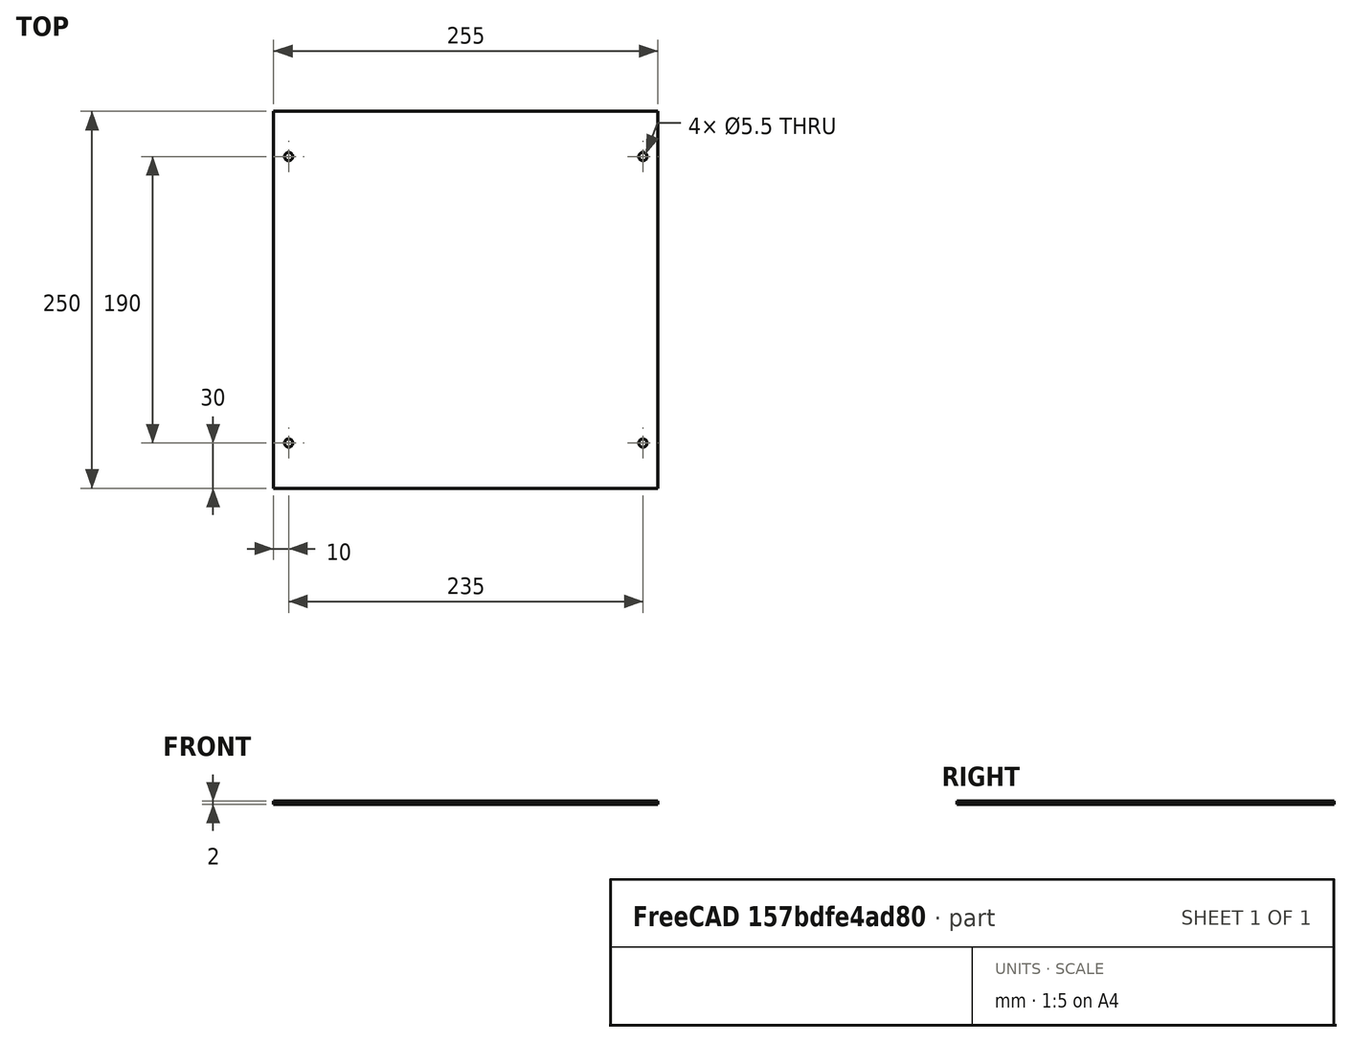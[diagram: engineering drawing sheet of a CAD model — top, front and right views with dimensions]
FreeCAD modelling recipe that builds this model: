
FCSTD DOCUMENT  (FreeCAD 0.15R4671 (Git))
Label: back
License: All rights reserved
LicenseURL: http://en.wikipedia.org/wiki/All_rights_reserved
objects: Drawing::FeatureViewPython×5, Part::Cylinder×4, Part::Cut×4, Part::Box×1, Drawing::FeatureViewPart×1, Drawing::FeaturePage×1
note: 9 computed .brp shape members not serialized (recipe doc carries the construction recipe); baked Part::Feature solids carry a one-line shape summary decoded from their .brp

FEATURE [Part::Box] Box001  label="Cube001"
  Height = 2
  Length = 255
  Placement = pos=(0,0,1.5332e-08) rot=(0,0,1;0rad)
  Width = 250
FEATURE [Part::Cylinder] Cylinder004
  Angle = 360
  Height = 10
  Placement = pos=(10,30,-5) rot=(0,0,1;0rad)
  Radius = 2.75
FEATURE [Part::Cylinder] Cylinder005
  Angle = 360
  Height = 10
  Placement = pos=(10,220,-5) rot=(0,0,1;0rad)
  Radius = 2.75
FEATURE [Part::Cylinder] Cylinder006
  Angle = 360
  Height = 10
  Placement = pos=(245,30,-5) rot=(0,0,1;0rad)
  Radius = 2.75
FEATURE [Part::Cylinder] Cylinder007
  Angle = 360
  Height = 10
  Placement = pos=(245,220,-5) rot=(0,0,1;0rad)
  Radius = 2.75
FEATURE [Part::Cut] Cut004
  Base = -> Box001
  Tool = -> Cylinder004
FEATURE [Part::Cut] Cut005
  Base = -> Cut004
  Tool = -> Cylinder005
FEATURE [Part::Cut] Cut006
  Base = -> Cut005
  Tool = -> Cylinder006
FEATURE [Part::Cut] Cut007  label="back"
  Base = -> Cut006
  Tool = -> Cylinder007
FEATURE [Drawing::FeatureViewPart] Ortho  label="Ortho_0_0"
  Direction = (0,0,-1)
  HiddenWidth = 0.15
  LineWidth = 0.35
  Rotation = 180
  Scale = 0.5
  ShowHiddenLines = false
  ShowSmoothLines = false
  Source = -> Cut007
  Tolerance = 0.05
  ViewResult = <g id="Ortho_0_0"\n   transform="rotate(180,46.25,56) translate(46.25,56) scale(0.5,0.5)"\n  >\n<g   stroke="rgb(0, 0, 0)"\n   stroke-width="0.7"\n   stroke-linecap="butt"\n   stroke-linejoin="miter"\n   fill="none"\n   transform="scale(1,-1)"\n  >\n<path id= "1" d=" M 0 0 L 0 250 " />\n<path id= "2" d=" M 0 0 L -255 0 " />\n<path id= "3" d=" M 0 250 L -255 250 " />\n<path id= "4" d=" M -255 0 L -255 250 " />\n<circle cx ="-245" cy ="220" r ="2.75" /><circle cx ="-10" cy ="220" r ="2.75" /><circle cx ="-245" cy ="30" r ="2.75" /><circle cx ="-10" cy ="30" r ="2.75" /></g>\n</g>
  Visible = true
  X = 46.25
  Y = 56
FEATURE [Drawing::FeatureViewPython] dimStack001  # drawing view (typed FeaturePython)
  Rotation = 0
  ViewResult = <g> <line x1="51.250000" y1="169.375001" x2="51.250000" y2="198.365725" style="stroke:rgb(0,0,255);stroke-width:0.50" />\n<line x1="46.250000" y1="183.000001" x2="46.250000" y2="198.365725" style="stroke:rgb(0,0,255);stroke-width:0.50" />\n<line x1="51.250000" y1="197.365725" x2="46.250000" y2="197.365725" style="stroke:rgb(0,0,255);stroke-width:0.50" />\n<polygon points="51.250000,197.365725 54.250000,198.365725 55.250000,197.365725 54.250000,196.365725" style="fill:rgb(0,0,255);stroke:rgb(0,0,255);stroke-width:0" />\n<polygon points="46.250000,197.365725 43.250000,196.365725 42.250000,197.365725 43.250000,198.365725" style="fill:rgb(0,0,255);stroke:rgb(0,0,255);stroke-width:0" />\n<text x="48.750000" y="195.365725" font-family="inherit" font-size="3.6" fill="rgb(0,0,255)" text-anchor="middle" transform="rotate(0.000000 48.750000,195.365725)" >10</text> </g> 
  Visible = true
  X = 0
  Y = 0
  arrowL1 = 3
  arrowL2 = 1
  arrowW = 2
  arrow_scheme = 0
  autoPlaceOffset = 2
  click1_x = 47.0563
  click1_y = 197.366
  comma_decimal_place = false
  dimension_line_overshoot = 1
  gap_datum_points = 2
  lineColor = rgb(0,0,255)
  stack_offset = 7
  stack_offset0 = 0
  strokeWidth = 0.5
  textFormat_linear = %(value)f
  textRenderer_color = rgb(0,0,255)
  textRenderer_family = inherit
  textRenderer_size = 3.6
  unit_custom_scale = 1
  unit_scheme = 0
FEATURE [Drawing::FeatureViewPython] dimStack002  # drawing view (typed FeaturePython)
  Rotation = 0
  ViewResult = <g> <line x1="49.249999" y1="166.000000" x2="33.981770" y2="166.000000" style="stroke:rgb(0,0,255);stroke-width:0.50" />\n<line x1="44.249999" y1="181.000000" x2="33.981770" y2="181.000000" style="stroke:rgb(0,0,255);stroke-width:0.50" />\n<line x1="34.981770" y1="166.000000" x2="34.981770" y2="181.000000" style="stroke:rgb(0,0,255);stroke-width:0.50" />\n<polygon points="34.981770,166.000000 33.981770,169.000000 34.981770,170.000000 35.981770,169.000000" style="fill:rgb(0,0,255);stroke:rgb(0,0,255);stroke-width:0" />\n<polygon points="34.981770,181.000000 35.981770,178.000000 34.981770,177.000000 33.981770,178.000000" style="fill:rgb(0,0,255);stroke:rgb(0,0,255);stroke-width:0" />\n<text x="32.981770" y="173.500000" font-family="inherit" font-size="3.6" fill="rgb(0,0,255)" text-anchor="middle" transform="rotate(-90.000000 32.981770,173.500000)" >30</text> </g> 
  Visible = true
  X = 0
  Y = 0
  arrowL1 = 3
  arrowL2 = 1
  arrowW = 2
  arrow_scheme = 0
  autoPlaceOffset = 2
  click1_x = 34.9818
  click1_y = 177.703
  comma_decimal_place = false
  dimension_line_overshoot = 1
  gap_datum_points = 2
  lineColor = rgb(0,0,255)
  stack_offset = 7
  stack_offset0 = 0
  strokeWidth = 0.5
  textFormat_linear = %(value)f
  textRenderer_color = rgb(0,0,255)
  textRenderer_family = inherit
  textRenderer_size = 3.6
  unit_custom_scale = 1
  unit_scheme = 0
FEATURE [Drawing::FeatureViewPython] dia001  # drawing view (typed FeaturePython)
  Rotation = 0
  ViewResult = <g>  <circle cx ="51.250000" cy ="71.000000" r="0.250000" stroke="none" fill="rgb(0,0,255)" /> \n<line x1="73.427542" y1="70.089927" x2="49.876156" y2="71.056377" style="stroke:rgb(0,0,255);stroke-width:0.50" />\n<polygon points="52.623844,70.943623 55.662322,71.819778 56.620480,70.779618 55.580320,69.821460" style="fill:rgb(0,0,255);stroke:rgb(0,0,255);stroke-width:0" />\n<polygon points="49.876156,71.056377 46.837678,70.180222 45.879520,71.220382 46.919680,72.178540" style="fill:rgb(0,0,255);stroke:rgb(0,0,255);stroke-width:0" />\n<line x1="73.427542" y1="70.089927" x2="78.619389" y2="70.089927" style="stroke:rgb(0,0,255);stroke-width:0.50" />\n<text x="76.023466" y="68.089927" font-family="inherit" font-size="3.6" fill="rgb(0,0,255)" text-anchor="middle" transform="rotate(0.000000 76.023466,68.089927)" >Ø5.5</text> </g>
  Visible = true
  X = 0
  Y = 0
  arrowL1 = 3
  arrowL2 = 1
  arrowW = 2
  arrow_scheme = 0
  autoPlaceOffset = 2
  autoPlaceText = true
  centerPointDia = 0.5
  click1_x = 73.4275
  click1_y = 70.0899
  click2_x = 78.6194
  click2_y = 71.9442
  click3_x = 78.6194
  click3_y = 71.9442
  comma_decimal_place = false
  lineColor = rgb(0,0,255)
  strokeWidth = 0.5
  textFormat_circular = Ø%(value)3.3f
  textRenderer_color = rgb(0,0,255)
  textRenderer_family = inherit
  textRenderer_size = 3.6
  unit_custom_scale = 1
  unit_scheme = 0
FEATURE [Drawing::FeatureViewPython] dim001  # drawing view (typed FeaturePython)
  Rotation = 0
  ViewResult = <g> \n  <line x1="46.250000" y1="54.000000" x2="46.250000" y2="40.163925" style="stroke:rgb(0,0,255);stroke-width:0.50" />\n<line x1="173.750000" y1="54.000000" x2="173.750000" y2="40.163925" style="stroke:rgb(0,0,255);stroke-width:0.50" />\n<line x1="46.250000" y1="41.163925" x2="173.750000" y2="41.163925" style="stroke:rgb(0,0,255);stroke-width:0.50" /> \n  <polygon points="173.750000,41.163925 170.750000,40.163925 169.750000,41.163925 170.750000,42.163925" style="fill:rgb(0,0,255);stroke:rgb(0,0,255);stroke-width:0" /><polygon points="46.250000,41.163925 49.250000,42.163925 50.250000,41.163925 49.250000,40.163925" style="fill:rgb(0,0,255);stroke:rgb(0,0,255);stroke-width:0" /> \n  <text x="110.000000" y="39.163925" font-family="inherit" font-size="3.6" fill="rgb(0,0,255)" text-anchor="middle" transform="rotate(0.000000 110.000000,39.163925)" >255</text> </g>
  Visible = true
  X = 0
  Y = 0
  arrowL1 = 3
  arrowL2 = 1
  arrowW = 2
  arrow_scheme = 0
  autoPlaceOffset = 2
  autoPlaceText = true
  click1_x = 109.4
  click1_y = 41.1639
  click2_x = 109.4
  click2_y = 41.1639
  comma_decimal_place = false
  dimension_line_overshoot = 1
  gap_datum_points = 2
  halfDimension_linear = false
  lineColor = rgb(0,0,255)
  strokeWidth = 0.5
  textFormat_linear = %(value)f
  textRenderer_color = rgb(0,0,255)
  textRenderer_family = inherit
  textRenderer_size = 3.6
  unit_custom_scale = 1
  unit_scheme = 0
FEATURE [Drawing::FeatureViewPython] dim002  # drawing view (typed FeaturePython)
  Rotation = 0
  ViewResult = <g> \n  <line x1="44.250000" y1="56.000000" x2="25.330078" y2="56.000000" style="stroke:rgb(0,0,255);stroke-width:0.50" />\n<line x1="44.250000" y1="181.000000" x2="25.330078" y2="181.000000" style="stroke:rgb(0,0,255);stroke-width:0.50" />\n<line x1="26.330078" y1="56.000000" x2="26.330078" y2="181.000000" style="stroke:rgb(0,0,255);stroke-width:0.50" /> \n  <polygon points="26.330078,181.000000 27.330078,178.000000 26.330078,177.000000 25.330078,178.000000" style="fill:rgb(0,0,255);stroke:rgb(0,0,255);stroke-width:0" /><polygon points="26.330078,56.000000 25.330078,59.000000 26.330078,60.000000 27.330078,59.000000" style="fill:rgb(0,0,255);stroke:rgb(0,0,255);stroke-width:0" /> \n  <text x="24.330078" y="118.500000" font-family="inherit" font-size="3.6" fill="rgb(0,0,255)" text-anchor="middle" transform="rotate(-90.000000 24.330078,118.500000)" >250</text> </g>
  Visible = true
  X = 0
  Y = 0
  arrowL1 = 3
  arrowL2 = 1
  arrowW = 2
  arrow_scheme = 0
  autoPlaceOffset = 2
  autoPlaceText = true
  click1_x = 26.3301
  click1_y = 117.929
  click2_x = 26.3301
  click2_y = 117.929
  comma_decimal_place = false
  dimension_line_overshoot = 1
  gap_datum_points = 2
  halfDimension_linear = false
  lineColor = rgb(0,0,255)
  strokeWidth = 0.5
  textFormat_linear = %(value)f
  textRenderer_color = rgb(0,0,255)
  textRenderer_family = inherit
  textRenderer_size = 3.6
  unit_custom_scale = 1
  unit_scheme = 0
FEATURE [Drawing::FeaturePage] Page
  EditableTexts = Fichou Dimitri | OCLab back | Aluminium - 2 mm thick | Professur für Lebensmittelwissenschaften | Prof. Dr. Gertrud Morlock | A4 | X / Y | SCALE | PART NUMBER | DRAWING NUMBER | YYYY-MM-DD | A
  Group = -> [Ortho,dimStack001,dimStack002,dia001,dim001,dim002]
  Template = <path>
note: 1 file-system path scrubbed to <path> (originals preserved in the JSON sidecar)
